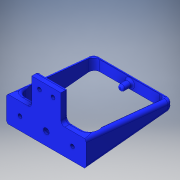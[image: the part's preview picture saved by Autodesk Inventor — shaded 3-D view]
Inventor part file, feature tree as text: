
AUTODESK INVENTOR PART (.ipt)
format: ipt  version: 2016 (Build 200138000, 138)  size: 442,368 bytes
history: native  units: in
note: dims shown in document units (in); Inventor stores cm internally (conversion verified against a paired STEP export)
features: sketch x10, fillet x10, extrude x7, hole x2
ambient origin geometry x8: Origin, YZ Plane, XZ Plane, XY Plane, X Axis, Y Axis, Z Axis, Center Point
bodies: Solid1 (feature_tree)
feature tree (29):
  extrude  "Extrusion1"  Depth=0.5197in
  extrude  "Extrusion11"  Depth=0.5118in
  sketch  "Sketch17"  dims[d84=0.5118in d85=0.562in d86=0.0in]
  sketch  "Sketch19"  dims[d87=0.1575in d88=0.4331in]
  sketch  "Sketch20"  dims[d89=0.2598in d90=0.2598in d91=0.2756in]
  extrude  "Extrusion13"  Depth=0.562in TaperAngle=0.0deg
  extrude  "Extrusion15"  Depth=0.4331in
  extrude  "Extrusion16"  Depth=0.2598in
  fillet  "Fillet29"  Radius=0.2756in
  extrude  "Extrusion17"  Depth=0.2598in
  fillet  "Fillet34"  Radius=0.2598in
  fillet  "Fillet35"  Radius=0.2756in
  fillet  "Fillet36"  Radius=0.0787in
  fillet  "Fillet37"  Radius=0.0787in
  fillet  "Fillet38"  Radius=1.6142in
  fillet  "Fillet39"  Radius=0.5197in
  fillet  "Fillet40"  Radius=0.5197in
  fillet  "Fillet41"  Radius=0.1969in
  hole  "Hole4"  [1 undecoded]
  sketch  "Sketch32"  dims[d154=0.0787in d155=1.4567in d156=0.0in d162=0.1575in d170=0.8071in d171=0.0984in d172=0.0984in d173=0.8071in d174=0.1181in d175=0.1969in d176=0.0in d177=0.0394in d178=0.0394in d179=0.1181in d180=0.0748in d181=0.1181in d182=0.0591in d183=0.0787in d184=0.0669in d185=0.0787in d186=0.2362in d187=0.1181in d188=0.0394in d189=90.0deg d190=0.1575in d191=0.8108in d193=0.0787in d194=0.0in d195=0.0787in d196=0.2362in d197=0.1575in d198=0.0787in d199=90.0deg d200=0.315in d201=0.8108in d202=0.1575in d203=0.1575in d204=0.0551in]
  extrude  "Extrusion18"  Depth=0.0787in
  hole  "Hole5"  [1 undecoded]
  fillet  "Fillet43"  Radius=0.1575in
  sketch  "Sketch1"  dims[d0=1.6142in d1=0.5197in]
  sketch  "Sketch16"  dims[d2=0.1575in d3=0.0in d83=0.5118in]
  sketch  "Sketch24"  dims[d92=0.1575in d96=0.2598in d97=0.2598in d98=0.2756in]
  sketch  "Sketch25"  dims[d108=0.2835in d110=0.2605in d111=0.2605in d112=0.3622in d113=0.1437in d114=0.5551in d115=0.2224in d116=0.0787in d133=0.0787in d134=0.0787in d135=1.6142in d136=0.0in d144=0.5197in d145=0.5197in d147=0.1969in]
  sketch  "Sketch30"  dims[d148=0.1614in d149=0.1614in]
  sketch  "Sketch31"  dims[d150=11.811in d151=0.0in d153=0.0787in]
note: 2 required parameter values undecoded (feature->parameter linkage not recoverable at this tier; creation-order binding heuristic only, values carry confidence <= 0.55)
